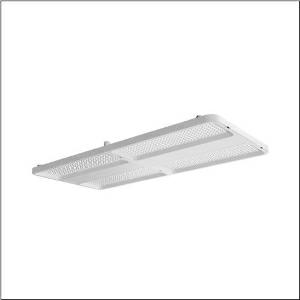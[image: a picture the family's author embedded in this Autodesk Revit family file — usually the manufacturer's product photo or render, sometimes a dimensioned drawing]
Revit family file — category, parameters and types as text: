
# Revit family: highbay_11_maxi_51hn11db4vda
name_source: partatom
category: Lighting Fixtures
units: mm (PartAtom-declared; Revit-internal decimal feet)

## family parameters
Cut with Voids When Loaded = No
Host = Face
Light Source = No
Part Type = Normal
Room Calculation Point = No
Round Connector Dimension = Use Diameter
Shared = No

## types (1)
- --- (1 x LED, 9070 lm, 44.6 W, 4000K)
    Apparent Load = 45 VA
    CIE Flux Codes = 85 97 100 100 100
    Color Rendering = 80
    Color Temperature = 4000K
    Default Elevation = 1800 mm
    Description = high bay luminaire Highbay 11 maxi; direct symmetric narrow distribution, light control with lens of PMMA; UGR ≤ 22 (X = 4H | Y = 8H | S = 0.25H | reflection values 70/50/20); luminous flux: 56.000lm; light colour: 840, colour temperature: 4000K, MacAdam ≤ 2 SDCM (initial), colour rendering: CRI > 80; luminous efficacy: 189,9lm/W; rated service life: 100.000h (L95) at AT= 25°C; control: DALI 2; luminaire connection: terminal, 5-pole, max. 2.5mm² (cable entry for one cable, Ø 8.5..16mm); mains connection: 230..240V, AC/DC 0/50..60Hz; connected load: 294,9W; protection rating (complete): IP66; insulation class (complete): insulation class I (protective earthing); protection symbol: D; impact resistance: IK08; certification: CE, ENEC, VDE, UKCA; luminaire for central battery installations according to EN 60598-2-22, internal wiring halogen-free; luminaire Suitable for use in the food industry according to the specifications of IFS-Food, HACCP and/or BRC; LABS conformity tested according to VDMA 24364:2018-05; housing frame of high-performance plastic PA6, matt traffic white (RAL 9016); cover of PMMA; dimension (LxWxH): 946 x 442 x 72mm; permissible operating ambient temperature: -40..+50°C (reducing of maximum allowable ambient temperature of 5°C with ceiling mounting); packaging unit: 1 piece; (delivery without accessories; please order mounting accessories separately)
    Height = 72 mm  [stored 0.23622 ft]
    Lamp = 1 x LED
    Lamp Light Flux = 9070 lm
    Lamp Power = 44.6 W
    Lamp count = 1
    Length = 946 mm
    Luminous efficacy = 203 lm/W
    Manufacturer = Siteco
    ModVariant = No
    Model = 51HN11DB4VDA
    Mounting Place = Ceiling
    Mounting Type = Pendant
    Number of Poles = 1
    OnlyDefault = Yes
    Power Factor = 1
    Product Name = Highbay 11 maxi
    Product group = high bay luminaire
    ProductGroupID = 902
    Protection Class = Protection class I
    Protection Degree = IP 66
    RLX_Detail_Level = 1
    RLX_Emergency_Light_Flux = 0 lm
    RLX_Emergency_Type = 0
    RLX_Emergency_Type_DB = No
    RlxData = <blob elided: 127421 chars, md5=6909a799>
    Socket = socket
    Standby Power = 0 W
    System Light Flux = 9070 lm
    System Power = 45 W
    Type Comments = : DC mode (central or group accumulator) initial emergency light level
    Type Image = l_1363244.jpg
    URL = http://relux.com
    VarID = @adj_022127
    Voltage = 0 V
    Weight = 0.00 kg
    Width = 442 mm

note: [stored X ft] marks values corroborated as IEEE doubles in the binary element streams (Revit-internal decimal feet)

## geometry (parser evidence)
native form markers: Blend x4, Sweep x11
no freeform markers — native parametric forms only
